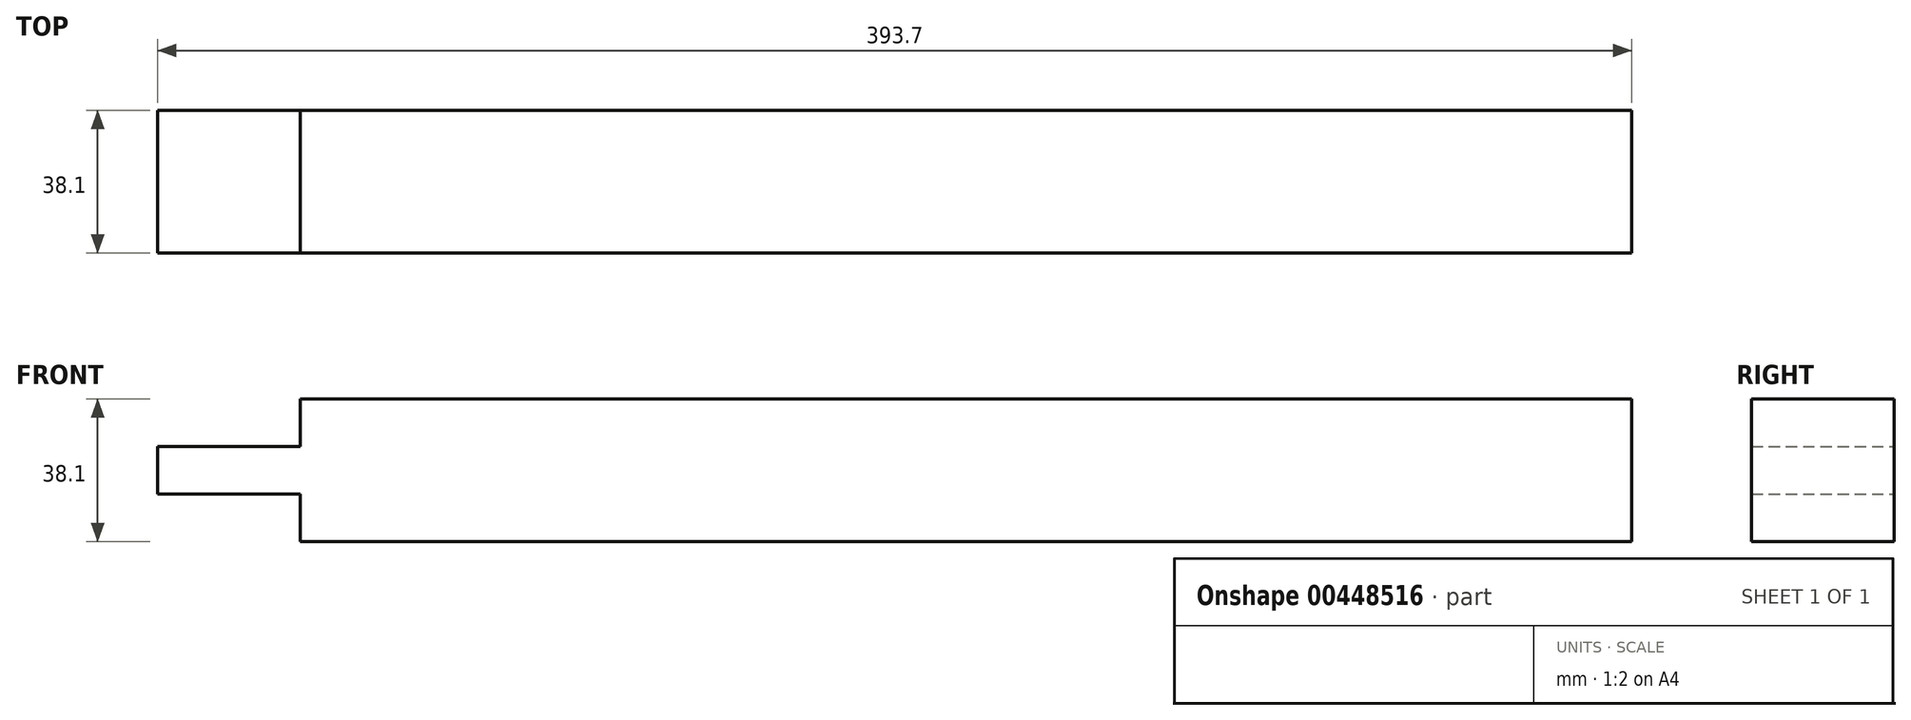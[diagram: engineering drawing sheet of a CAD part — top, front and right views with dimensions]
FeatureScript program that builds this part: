
annotation { "Feature Type Name" : "Feature", "Feature Type Description" : "" }
export const myFeature = defineFeature(function(context is Context, id is Id, definition is map)
    precondition{}
    {
        {
            var Q0;
            Q0=qCreatedBy(makeId("Front.planeOp"),FACE);
            var sketch = newSketch(context, id + "F0", { "sketchPlane" : qUnion([Q0])});
            skLineSegment(sketch, "E0.bottom", {"start": v(38.1, 0) * mm, "end": v(393.7, 0) * mm});
            skLineSegment(sketch, "E0.top", {"start": v(38.1, -38.1) * mm, "end": v(393.7, -38.1) * mm});
            skLineSegment(sketch, "E0.right", {"start": v(393.7, 0) * mm, "end": v(393.7, -38.1) * mm});
            skLineSegment(sketch, "E1", {"start": v(0, -12.7) * mm, "end": v(38.1, -12.7) * mm});
            skLineSegment(sketch, "E2", {"start": v(38.1, -25.4) * mm, "end": v(0, -25.4) * mm});
            skLineSegment(sketch, "E3", {"start": v(38.1, -12.7) * mm, "end": v(38.1, 0) * mm});
            skLineSegment(sketch, "E4", {"start": v(38.1, 0) * mm, "end": v(38.1, -12.7) * mm});
            skLineSegment(sketch, "E5", {"start": v(38.1, -25.4) * mm, "end": v(38.1, -38.1) * mm});
            skLineSegment(sketch, "E6", {"start": v(0, -12.7) * mm, "end": v(0, -25.4) * mm});
            skSolve(sketch);
        }
        {
            var Q0;
            Q0=makeQuery(id+"F0.imprint","IMPRINT",FACE,{"disambiguationData":[TD([[makeQuery(id+"F0.imprint","IMPRINT",EDGE,{"derivedFrom":sQuery(id+"F0.wireOp",EDGE,"E0.bottom")}),-1.0]])]});
            extrude(context, id + "F1", {"entities" : qUnion([Q0]), "depth" : 38.1 * mm});
        }
    });
